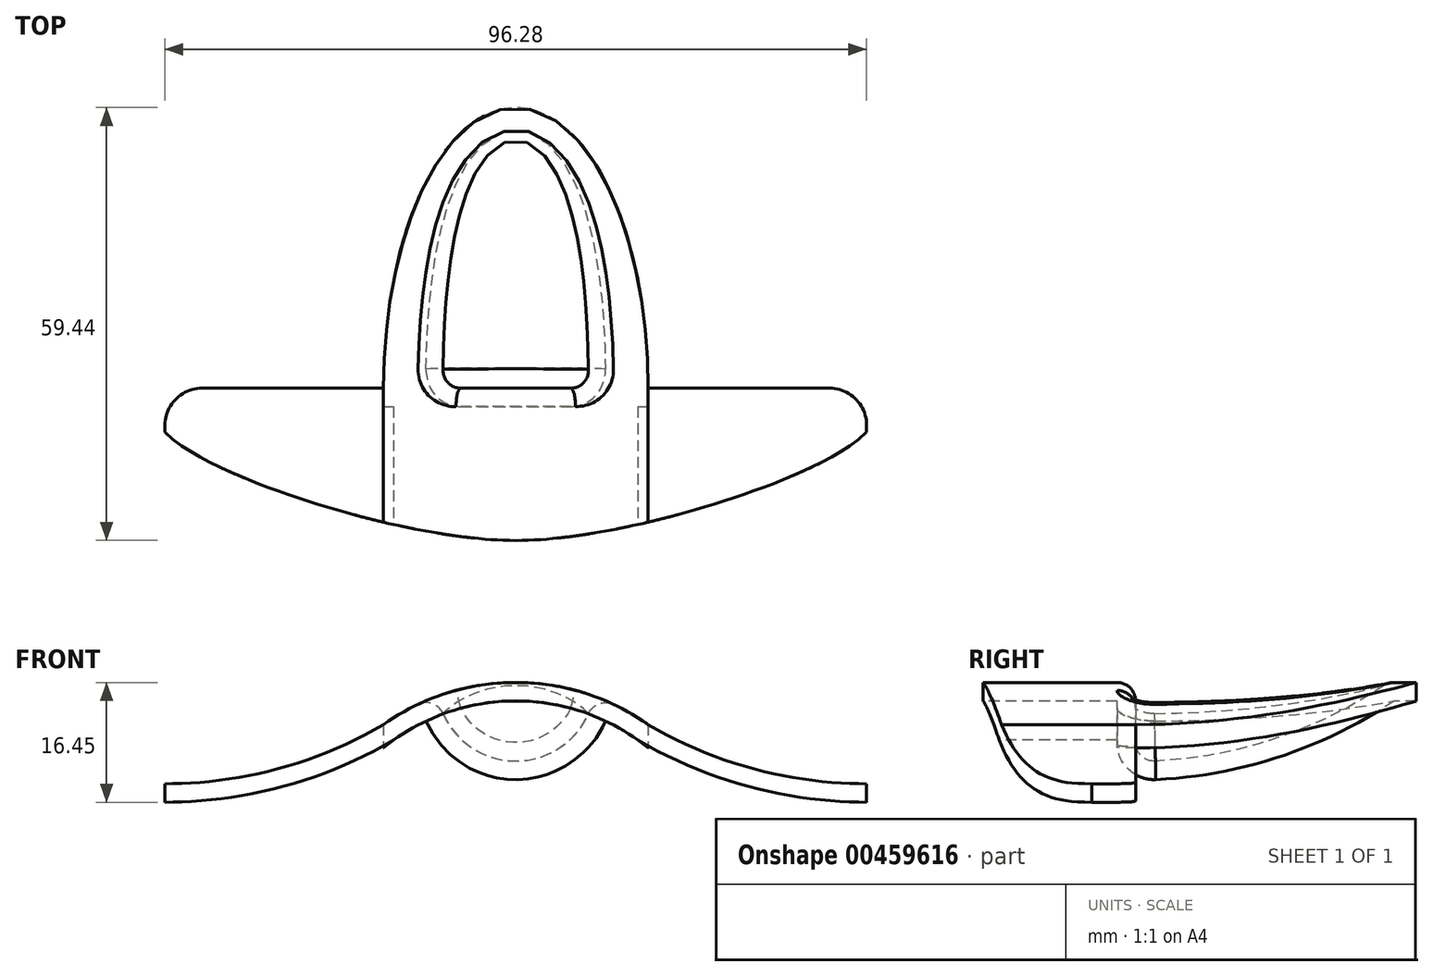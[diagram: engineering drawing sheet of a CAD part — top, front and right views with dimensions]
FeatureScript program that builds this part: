
annotation { "Feature Type Name" : "Feature", "Feature Type Description" : "" }
export const myFeature = defineFeature(function(context is Context, id is Id, definition is map)
    precondition{}
    {
        {
            var Q0;
            Q0=qCreatedBy(makeId("Front.planeOp"),FACE);
            var sketch = newSketch(context, id + "F0", { "sketchPlane" : qUnion([Q0])});
            skArc(sketch, "E0", {"start": v(0, 20.6) * mm, "mid": v(-9.53, 19.11) * mm, "end": v(-18.15, 14.8) * mm});
            skArc(sketch, "E1", {"start": v(-48.14, 6.68) * mm, "mid": v(-32.6, 8.75) * mm, "end": v(-18.15, 14.8) * mm});
            skSolve(sketch);
        }
        {
            var Q0;
            Q0=sQuery(id+"F0.wireOp",EDGE,"E1");
            var Q1;
            Q1=sQuery(id+"F0.wireOp",EDGE,"E0");
            extrude(context, id + "F1", {"bodyType" : ToolBodyType.SURFACE, "surfaceEntities" : qUnion([Q0, Q1]), "depth" : 76.2 * mm});
        }
        {
            var Q0;
            Q0=qCreatedBy(makeId("Top.planeOp"),FACE);
            var sketch = newSketch(context, id + "F2", { "sketchPlane" : qUnion([Q0])});
            skFitSpline(sketch, "E2", {"points": [v(0, -20.91) * mm, v(-48.14, -6) * mm], "startDerivative": vector(-46.95, 0) * mm, "endDerivative": vector(-15.95, 17.98) * mm});
            skLineSegment(sketch, "E3", {"start": v(-48.14, -6) * mm, "end": v(-48.14, 0) * mm});
            skLineSegment(sketch, "E4", {"start": v(-48.14, 0) * mm, "end": v(0, 0) * mm});
            skLineSegment(sketch, "E5", {"start": v(0, 0) * mm, "end": v(0, -20.91) * mm});
            skSolve(sketch);
        }
        {
            var Q0;
            Q0 = qSketchRegion(id + "F2", true);
            extrude(context, id + "F3", {"entities" : qUnion([Q0]), "endBound" : BoundingType.UP_TO_NEXT, "depth" : 25.4 * mm});
        }
        {
            var Q0;
            Q0=makeQuery(id+"F3.opExtrude","SWEPT_FACE",FACE,{"disambiguationData":[OSD([sQuery(id+"F2.wireOp",EDGE,"E5")])]});
            var Q1;
            Q1=makeQuery(id+"F3.opExtrude","SWEPT_FACE",FACE,{"disambiguationData":[OSD([sQuery(id+"F2.wireOp",EDGE,"E2")])]});
            var Q2;
            Q2=makeQuery(id+"F3.opExtrude","SWEPT_FACE",FACE,{"disambiguationData":[OSD([sQuery(id+"F2.wireOp",EDGE,"E4")])]});
            var Q3;
            Q3=makeQuery(id+"F3.opExtrude","CAP_FACE",FACE,{"disambiguationData":[OSD([sQuery(id+"F2.wireOp",EDGE,"E2"),sQuery(id+"F2.wireOp",EDGE,"E3"),sQuery(id+"F2.wireOp",EDGE,"E4"),sQuery(id+"F2.wireOp",EDGE,"E5")])],"isStart":true});
            var Q4;
            Q4=makeQuery(id+"F3.opExtrude","SWEPT_FACE",FACE,{"disambiguationData":[OSD([sQuery(id+"F2.wireOp",EDGE,"E3")])]});
            shell(context, id + "F4", {"entities" : qUnion([Q0, Q1, Q2, Q3, Q4]), "thickness" : 2.54 * mm});
        }
        {
            var Q0;
            Q0=makeQuery(id+"F3.opExtrude","SWEPT_BODY",BODY,{"disambiguationData":[OSD([sQuery(id+"F2.wireOp",EDGE,"E2"),sQuery(id+"F2.wireOp",EDGE,"E3"),sQuery(id+"F2.wireOp",EDGE,"E4"),sQuery(id+"F2.wireOp",EDGE,"E5")])]});
            var Q1;
            Q1=qCreatedBy(makeId("Right.planeOp"),FACE);
            mirror(context, id + "F5", {"operationType" : NewBodyOperationType.ADD, "entities" : qUnion([Q0]), "mirrorPlane" : qUnion([Q1])});
        }
        {
            var Q0;
            Q0=qCreatedBy(makeId("Top.planeOp"),FACE);
            var sketch = newSketch(context, id + "F6", { "sketchPlane" : qUnion([Q0])});
            skEllipse(sketch, "E6", {"center": v(0, 0) * mm, "majorRadius": 38.53 * mm, "minorRadius": 18.15 * mm, "majorAxis": v(0, 1)});
            skLineSegment(sketch, "E7", {"start": v(-18.15, 0) * mm, "end": v(18.15, 0) * mm});
            skLineSegment(sketch, "E8", {"start": v(-18.11, -2.54) * mm, "end": v(18.11, -2.54) * mm});
            skSolve(sketch);
        }
        {
            var Q0;
            {var subQ0=sQuery(id+"F6.wireOp",EDGE,"E7");Q0=makeQuery(id+"F6.imprint","IMPRINT",FACE,{"disambiguationData":[TD([[makeQuery(id+"F6.imprint","IMPRINT",EDGE,{"derivedFrom":subQ0}),1.0]])]});}
            var Q1;
            {var subQ0=sQuery(id+"F6.wireOp",EDGE,"E7");Q1=makeQuery(id+"F6.imprint","IMPRINT",FACE,{"disambiguationData":[TD([[makeQuery(id+"F6.imprint","IMPRINT",EDGE,{"derivedFrom":subQ0}),-1.0]])]});}
            var Q2;
            {var subQ0=makeQuery(id+"F3.opExtrude","CAP_FACE",FACE,{"disambiguationData":[OSD([sQuery(id+"F2.wireOp",EDGE,"E2"),sQuery(id+"F2.wireOp",EDGE,"E3"),sQuery(id+"F2.wireOp",EDGE,"E4"),sQuery(id+"F2.wireOp",EDGE,"E5")]),topologyDisambiguationEdgeConnected([makeQuery(id+"F1.opExtrude","SWEPT_FACE",FACE,{"disambiguationData":[OSD([sQuery(id+"F0.wireOp",EDGE,"E0")])]})])],"isStart":false});Q2=makeQuery(id+"F5.boolean.opBoolean","MERGE",FACE,{"derivedFrom":[subQ0,makeQuery(id+"F5.opPattern","COPY",FACE,{"derivedFrom":subQ0,"instanceName":"1"})]});}
            extrude(context, id + "F7", {"entities" : qUnion([Q0, Q1]), "operationType" : NewBodyOperationType.ADD, "endBound" : BoundingType.UP_TO_SURFACE, "endBoundEntityFace" : qUnion([Q2]), "depth" : 25.4 * mm});
        }
        {
            var Q0;
            Q0=qCreatedBy(makeId("Front.planeOp"),FACE);
            var sketch = newSketch(context, id + "F8", { "sketchPlane" : qUnion([Q0])});
            skCircle(sketch, "E9", {"center": v(0, 20.65) * mm, "radius": 10.91 * mm});
            skSolve(sketch);
        }
        {
            var Q0;
            Q0=qCreatedBy(makeId("Right.planeOp"),FACE);
            var sketch = newSketch(context, id + "F9", { "sketchPlane" : qUnion([Q0])});
            skFitSpline(sketch, "E10", {"points": [v(0, 20.58) * mm, v(32.71, 32.7) * mm], "startDerivative": vector(33.82, 0) * mm, "endDerivative": vector(28.94, 24.44) * mm});
            skSolve(sketch);
        }
        {
            var Q0;
            Q0=makeQuery(id+"F8.imprint","IMPRINT",FACE,{"disambiguationData":[TD([[makeQuery(id+"F8.imprint","IMPRINT",EDGE,{"derivedFrom":sQuery(id+"F8.wireOp",EDGE,"E9")}),1.0]])]});
            var Q1;
            Q1=sQuery(id+"F9.wireOp",EDGE,"E10");
            sweep(context, id + "F10", {"operationType" : NewBodyOperationType.REMOVE, "profiles" : qUnion([Q0]), "path" : qUnion([Q1])});
        }
        {
            var Q0;
            Q0=makeQuery(id+"F7.opExtrude","SWEPT_FACE",FACE,{"disambiguationData":[OSD([sQuery(id+"F6.wireOp",EDGE,"E6")])]});
            var Q1;
            Q1=makeQuery(id+"F7.opExtrude","CAP_FACE",FACE,{"disambiguationData":[OSD([sQuery(id+"F6.wireOp",EDGE,"E6"),sQuery(id+"F6.wireOp",EDGE,"E8")])],"isStart":true});
            var Q2;
            Q2=makeQuery(id+"F7.opExtrude","SWEPT_FACE",FACE,{"disambiguationData":[OSD([sQuery(id+"F6.wireOp",EDGE,"E7")])]});
            var Q3;
            Q3=makeQuery(id+"F7.opExtrude","SWEPT_FACE",FACE,{"disambiguationData":[OSD([sQuery(id+"F6.wireOp",EDGE,"E8")])]});
            shell(context, id + "F11", {"entities" : qUnion([Q0, Q1, Q2, Q3]), "thickness" : 2.54 * mm});
        }
        {
            var Q0;
            Q0=makeQuery(id+"F10.boolean.opBoolean","COPY",EDGE,{"derivedFrom":makeQuery(id+"F10.opSweep","CAP_EDGE",EDGE,{"disambiguationData":[OSD([sQuery(id+"F8.wireOp",EDGE,"E9"),sQuery(id+"F9.wireOp",VERTEX,"E10.start")])],"isStart":true})});
            fillet(context, id + "F12", {"entities" : qUnion([Q0]), "radius" : 2.54 * mm, "tangentPropagation" : true, "allowEdgeOverflow" : false});
        }
        {
            var Q0;
            Q0=makeQuery(id+"F11.opShell","OFFSET_EDGE",EDGE,{"disambiguationData":[OSD([sQuery(id+"F8.wireOp",EDGE,"E9"),sQuery(id+"F9.wireOp",VERTEX,"E10.start")])]});
            fillet(context, id + "F13", {"entities" : qUnion([Q0]), "radius" : 5.08 * mm, "tangentPropagation" : true, "allowEdgeOverflow" : false});
        }
        {
            var Q0;
            Q0=makeQuery(id+"F5.opPattern","COPY",EDGE,{"derivedFrom":makeQuery(id+"F3.opExtrude","SWEPT_EDGE",EDGE,{"disambiguationData":[OSD([sQuery(id+"F2.wireOp",EDGE,"E3"),sQuery(id+"F2.wireOp",EDGE,"E4")])]}),"instanceName":"1"});
            var Q1;
            Q1=makeQuery(id+"F3.opExtrude","SWEPT_EDGE",EDGE,{"disambiguationData":[OSD([sQuery(id+"F2.wireOp",EDGE,"E3"),sQuery(id+"F2.wireOp",EDGE,"E4")])]});
            fillet(context, id + "F14", {"entities" : qUnion([Q0, Q1]), "radius" : 5.08 * mm, "tangentPropagation" : true, "allowEdgeOverflow" : false});
        }
        {
            var Q0;
            {var subQ0=makeQuery(id+"F3.opExtrude","CAP_FACE",FACE,{"disambiguationData":[OSD([sQuery(id+"F2.wireOp",EDGE,"E2"),sQuery(id+"F2.wireOp",EDGE,"E3"),sQuery(id+"F2.wireOp",EDGE,"E4"),sQuery(id+"F2.wireOp",EDGE,"E5")]),topologyDisambiguationEdgeConnected([makeQuery(id+"F1.opExtrude","SWEPT_FACE",FACE,{"disambiguationData":[OSD([sQuery(id+"F0.wireOp",EDGE,"E0")])]})])],"isStart":false});Q0=makeQuery(id+"F10.boolean.opBoolean","INTERSECT",EDGE,{"derivedFrom":[makeQuery(id+"F7.boolean.opBoolean","MERGE",FACE,{"derivedFrom":[makeQuery(id+"F5.boolean.opBoolean","MERGE",FACE,{"derivedFrom":[subQ0,makeQuery(id+"F5.opPattern","COPY",FACE,{"derivedFrom":subQ0,"instanceName":"1"})]}),makeQuery(id+"F7.opExtrude","CAP_FACE",FACE,{"disambiguationData":[OSD([sQuery(id+"F6.wireOp",EDGE,"E6"),sQuery(id+"F6.wireOp",EDGE,"E8")])],"isStart":false})]}),makeQuery(id+"F10.opSweep","CAP_FACE",FACE,{"disambiguationData":[OSD([sQuery(id+"F8.wireOp",EDGE,"E9"),sQuery(id+"F9.wireOp",VERTEX,"E10.start")])],"isStart":true})]});}
            fillet(context, id + "F15", {"entities" : qUnion([Q0]), "radius" : 2.54 * mm, "tangentPropagation" : true, "allowEdgeOverflow" : false});
        }
    });
